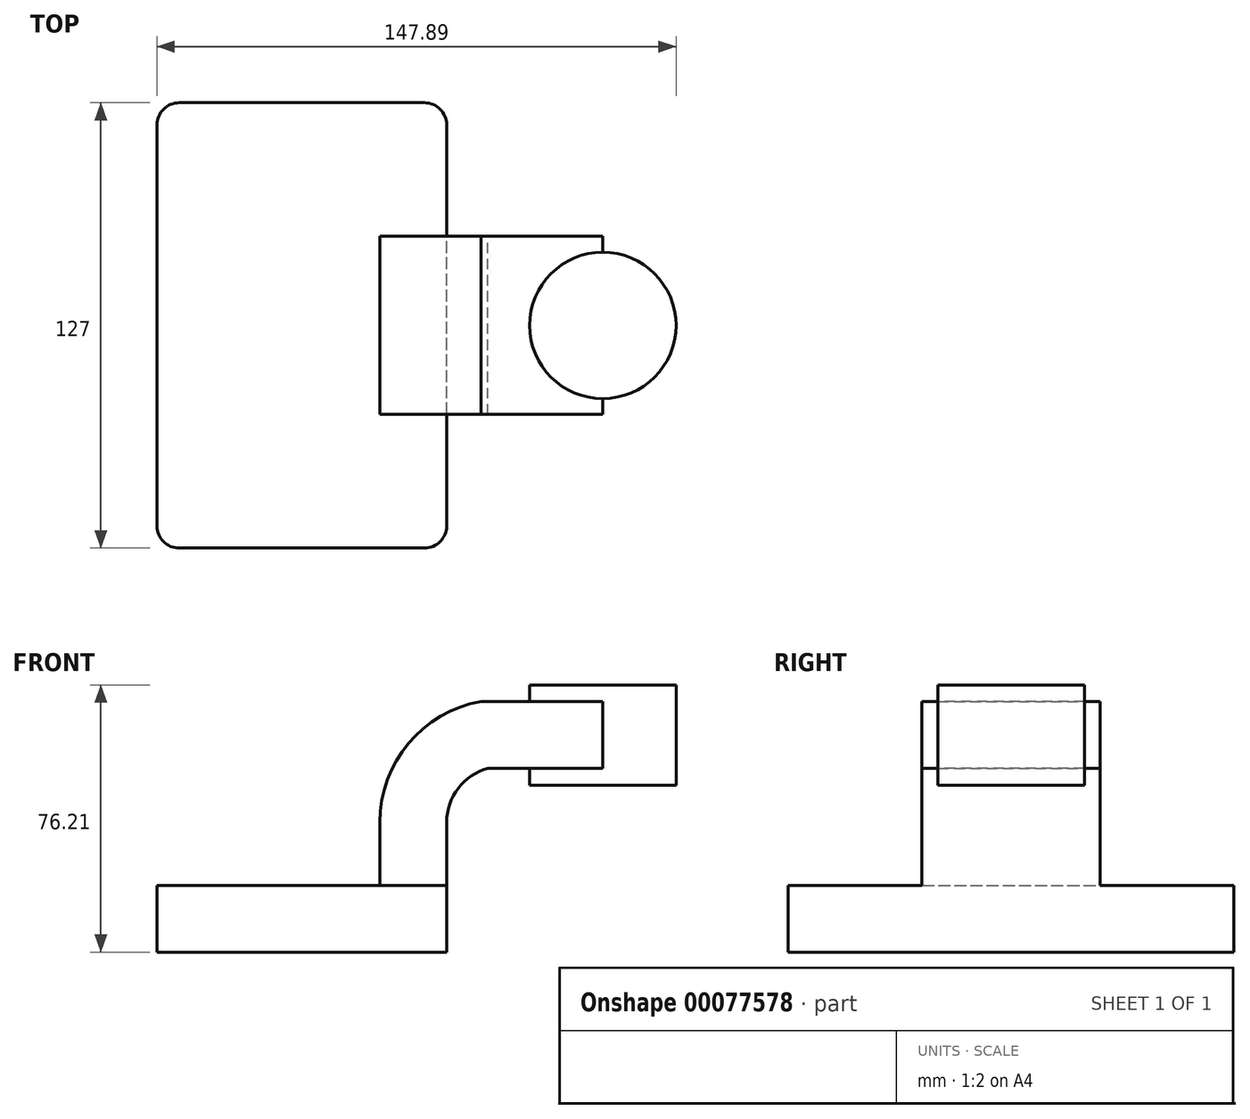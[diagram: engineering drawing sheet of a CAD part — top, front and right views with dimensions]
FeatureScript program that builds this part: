
annotation { "Feature Type Name" : "Feature", "Feature Type Description" : "" }
export const myFeature = defineFeature(function(context is Context, id is Id, definition is map)
    precondition{}
    {
        {
            var Q0;
            Q0=qCreatedBy(makeId("Front.planeOp"),FACE);
            var sketch = newSketch(context, id + "F0", { "sketchPlane" : qUnion([Q0])});
            skLineSegment(sketch, "E0.bottom", {"start": v(-41.28, -9.53) * mm, "end": v(41.28, -9.52) * mm});
            skLineSegment(sketch, "E0.top", {"start": v(-41.28, 9.52) * mm, "end": v(41.28, 9.53) * mm});
            skLineSegment(sketch, "E0.left", {"start": v(-41.28, -9.53) * mm, "end": v(-41.28, 9.52) * mm});
            skLineSegment(sketch, "E0.right", {"start": v(41.28, -9.52) * mm, "end": v(41.28, 9.53) * mm});
            skPoint(sketch, "E0.middle", {"position": v(0, 0) * mm});
            skLineSegment(sketch, "E1.bottom", {"start": v(55.82, 66.68) * mm, "end": v(106.62, 66.68) * mm});
            skLineSegment(sketch, "E1.top", {"start": v(55.82, 38.1) * mm, "end": v(106.62, 38.1) * mm});
            skLineSegment(sketch, "E1.left", {"start": v(55.82, 66.68) * mm, "end": v(55.82, 38.1) * mm});
            skLineSegment(sketch, "E1.right", {"start": v(106.62, 66.68) * mm, "end": v(106.62, 38.1) * mm});
            skLineSegment(sketch, "E2", {"start": v(41.28, 9.53) * mm, "end": v(41.28, 27.55) * mm});
            skArc(sketch, "E3", {"start": v(41.28, 27.55) * mm, "mid": v(44.55, 37.2) * mm, "end": v(53.02, 42.88) * mm});
            skLineSegment(sketch, "E4", {"start": v(53.02, 42.88) * mm, "end": v(85.75, 42.88) * mm});
            skPoint(sketch, "E5", {"position": v(85.72, 52.39) * mm});
            skLineSegment(sketch, "E6.0", {"start": v(51, 61.93) * mm, "end": v(85.75, 61.93) * mm});
            skArc(sketch, "E6.1", {"start": v(22.23, 27.55) * mm, "mid": v(30.37, 49.96) * mm, "end": v(51, 61.93) * mm});
            skLineSegment(sketch, "E6.2", {"start": v(22.23, 9.53) * mm, "end": v(22.23, 27.55) * mm});
            skLineSegment(sketch, "E7", {"start": v(85.75, 66.68) * mm, "end": v(85.75, 38.1) * mm});
            skFitSpline(sketch, "E8", {"points": [v(-41.28, 9.52) * mm, v(51, 61.93) * mm], "startDerivative": vector(-0.2, 79.78) * mm, "endDerivative": vector(128.27, 1.02) * mm});
            skSolve(sketch);
        }
        {
            var Q0;
            Q0=makeQuery(id+"F0.imprint","IMPRINT",FACE,{"disambiguationData":[TD([[makeQuery(id+"F0.imprint","IMPRINT",EDGE,{"derivedFrom":sQuery(id+"F0.wireOp",EDGE,"E0.bottom")}),1.0]])]});
            extrude(context, id + "F1", {"entities" : qUnion([Q0]), "endBound" : BoundingType.SYMMETRIC, "depth" : 127 * mm});
        }
        {
            var Q0;
            {var subQ1=sQuery(id+"F0.wireOp",EDGE,"E2");Q0=makeQuery(id+"F0.imprint","IMPRINT",FACE,{"disambiguationData":[TD([[makeQuery(id+"F0.imprint","IMPRINT",EDGE,{"derivedFrom":subQ1}),1.0]])]});}
            var Q1;
            {var subQ0=sQuery(id+"F0.wireOp",EDGE,"E6.0");var subQ1=sQuery(id+"F0.wireOp",EDGE,"E1.left");var subQ2=makeQuery(id+"F0.imprint","INTERSECT",VERTEX,{"derivedFrom":[subQ1,subQ0]});Q1=makeQuery(id+"F0.imprint","IMPRINT",FACE,{"disambiguationData":[TD([[makeQuery(id+"F0.imprint","IMPRINT",EDGE,{"disambiguationData":[TD([[subQ2,-1.0]])],"derivedFrom":subQ1}),1.0]])]});}
            extrude(context, id + "F2", {"entities" : qUnion([Q0, Q1]), "operationType" : NewBodyOperationType.ADD, "endBound" : BoundingType.SYMMETRIC, "depth" : 50.8 * mm});
        }
        {
            var Q0;
            Q0=makeQuery(id+"F0.imprint","IMPRINT",FACE,{"disambiguationData":[TD([[makeQuery(id+"F0.imprint","IMPRINT",EDGE,{"derivedFrom":sQuery(id+"F0.wireOp",EDGE,"E6.1")}),1.0]])]});
            extrude(context, id + "F3", {"entities" : qUnion([Q0]), "operationType" : NewBodyOperationType.ADD, "endBound" : BoundingType.SYMMETRIC, "depth" : 15.88 * mm});
        }
        {
            var Q0;
            {var subQ0=sQuery(id+"F0.wireOp",EDGE,"E1.right");Q0=makeQuery(id+"F0.imprint","IMPRINT",FACE,{"disambiguationData":[TD([[makeQuery(id+"F0.imprint","IMPRINT",EDGE,{"derivedFrom":subQ0}),-1.0]])]});}
            var Q1;
            Q1=sQuery(id+"F0.wireOp",EDGE,"E7");
            revolve(context, id + "F4", {"operationType" : NewBodyOperationType.ADD, "entities" : qUnion([Q0]), "axis" : qUnion([Q1]), "revolveType" : RevolveType.FULL});
        }
        {
            var Q0;
            Q0=makeQuery(id+"F1.opExtrude","CAP_EDGE",EDGE,{"disambiguationData":[OSD([sQuery(id+"F0.wireOp",EDGE,"E0.left")])],"isStart":false});
            var Q1;
            Q1=makeQuery(id+"F1.opExtrude","CAP_EDGE",EDGE,{"disambiguationData":[OSD([sQuery(id+"F0.wireOp",EDGE,"E0.right")])],"isStart":false});
            var Q2;
            Q2=makeQuery(id+"F1.opExtrude","CAP_EDGE",EDGE,{"disambiguationData":[OSD([sQuery(id+"F0.wireOp",EDGE,"E0.left")])],"isStart":true});
            var Q3;
            Q3=makeQuery(id+"F1.opExtrude","CAP_EDGE",EDGE,{"disambiguationData":[OSD([sQuery(id+"F0.wireOp",EDGE,"E0.right")])],"isStart":true});
            fillet(context, id + "F5", {"entities" : qUnion([Q0, Q1, Q2, Q3]), "radius" : 6.35 * mm, "tangentPropagation" : true, "allowEdgeOverflow" : false});
        }
        {
            var Q0;
            Q0=sQuery(id+"F0.wireOp",EDGE,"E1.right");
            var Q1;
            Q1=sQuery(id+"F0.wireOp",EDGE,"E7");
            revolve(context, id + "F6", {"bodyType" : ToolBodyType.SURFACE, "surfaceEntities" : qUnion([Q0]), "axis" : qUnion([Q1]), "revolveType" : RevolveType.FULL});
        }
    });
